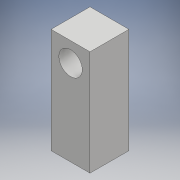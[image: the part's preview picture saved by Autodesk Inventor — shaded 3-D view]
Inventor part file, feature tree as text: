
AUTODESK INVENTOR PART (.ipt)
format: ipt  version: 2018 (Build 220112000, 112)  size: 106,496 bytes
history: native  units: mm
features: extrude x3, sketch x3
ambient origin geometry x8: Origin, YZ Plane, XZ Plane, XY Plane, X Axis, Y Axis, Z Axis, Center Point
bodies: Solid1 (feature_tree)
feature tree (6):
  extrude  "Extrusion1"  Depth=27.0mm
  extrude  "Extrusion2"  Depth=10.0mm
  extrude  "Extrusion3"  Depth=10.0mm TaperAngle=0.0deg
  sketch  "Sketch1"  dims[d0=10.0mm d1=27.0mm]
  sketch  "Sketch2"  dims[d2=10.0mm d3=0.0mm d4=5.0mm]
  sketch  "Sketch3"  dims[d5=6.0mm d6=10.0mm d7=0.0mm d8=5.0mm d9=5.0mm d10=3.9mm d11=15.0mm d12=0.0mm]
